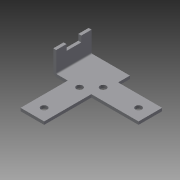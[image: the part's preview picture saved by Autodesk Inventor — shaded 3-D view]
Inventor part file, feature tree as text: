
AUTODESK INVENTOR PART (.ipt)
format: ipt  version: 2013 (Build 170138000, 138)  size: 125,440 bytes
history: native  units: in
note: dims shown in document units (in); Inventor stores cm internally (conversion verified against a paired STEP export)
features: sheet_metal_op x4, sketch x3, other x3
ambient origin geometry x8: Origin, YZ Plane, XZ Plane, XY Plane, X Axis, Y Axis, Z Axis, Center Point
bodies: Solid1 (feature_tree)
feature tree (10):
  sheet_metal_op  "Face1"
  sheet_metal_op  "Flange1"
  sketch  "Sketch1"  dims[d0=1.75in]
  other  "Plate1"
  sketch  "Sketch2"  dims[d1=0.125in]
  other  "Plate2"
  sheet_metal_op  "Bend1"
  sheet_metal_op  "Corner1"
  sketch  "Sketch3"  dims[d2=0.125in d3=0.0625in d4=0.25in d5=0.125in d6=1.0in d7=90.0deg d8=0.05in d9=0.5in d10=0.125in d11=0.125in d12=0.25in d13=0.625in d14=0.4375in d15=0.125in d16=0.0in]
  other  "Cut1"
